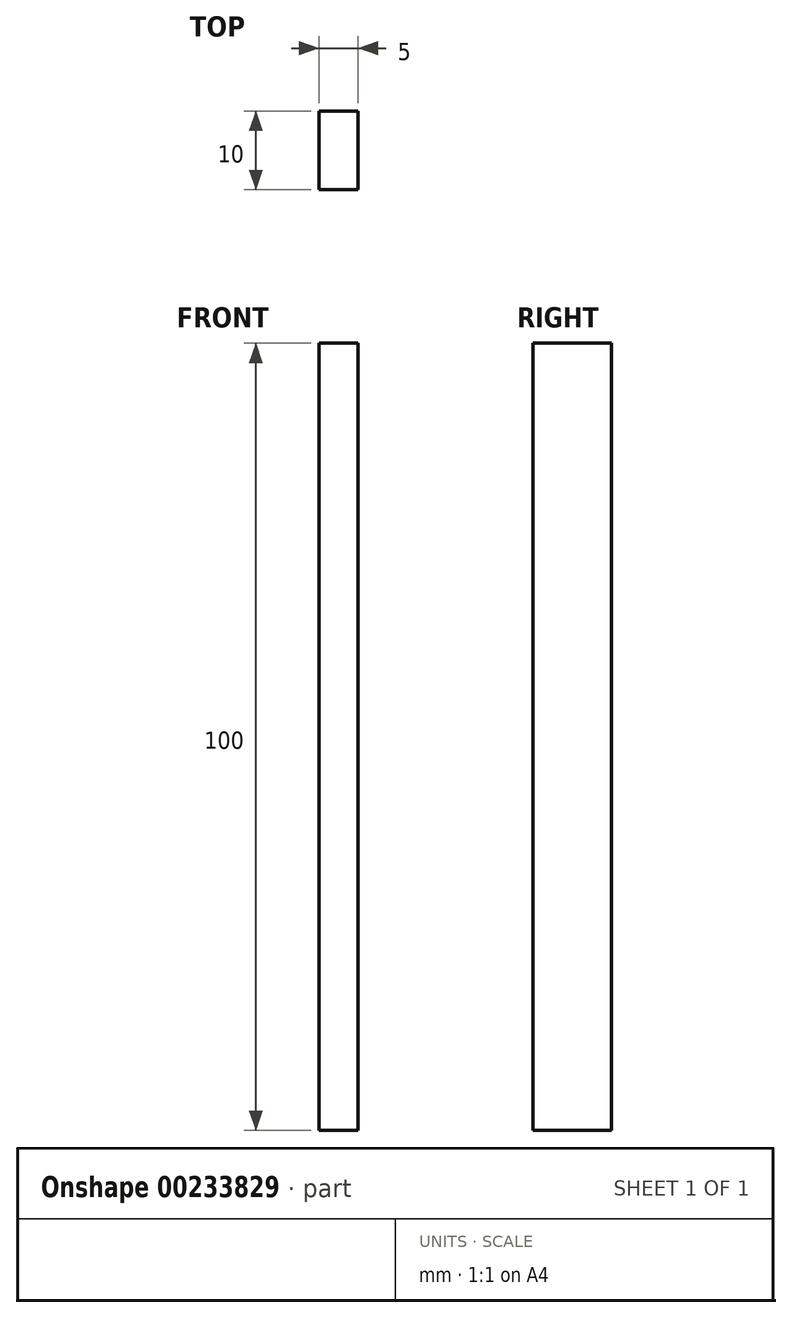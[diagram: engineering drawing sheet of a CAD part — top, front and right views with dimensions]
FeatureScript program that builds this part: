
annotation { "Feature Type Name" : "Feature", "Feature Type Description" : "" }
export const myFeature = defineFeature(function(context is Context, id is Id, definition is map)
    precondition{}
    {
        {
            var Q0;
            Q0=qCreatedBy(makeId("Front.planeOp"),FACE);
            var sketch = newSketch(context, id + "F0", { "sketchPlane" : qUnion([Q0])});
            skLineSegment(sketch, "E0.bottom", {"start": v(-5, 100) * mm, "end": v(0, 100) * mm});
            skLineSegment(sketch, "E0.top", {"start": v(-5, 0) * mm, "end": v(0, 0) * mm});
            skLineSegment(sketch, "E0.left", {"start": v(-5, 100) * mm, "end": v(-5, 0) * mm});
            skLineSegment(sketch, "E0.right", {"start": v(0, 100) * mm, "end": v(0, 0) * mm});
            skSolve(sketch);
        }
        {
            var Q0;
            Q0=makeQuery(id+"F0.imprint","IMPRINT",FACE,{"disambiguationData":[TD([[makeQuery(id+"F0.imprint","IMPRINT",EDGE,{"derivedFrom":sQuery(id+"F0.wireOp",EDGE,"E0.bottom")}),-1.0]])]});
            extrude(context, id + "F1", {"entities" : qUnion([Q0]), "depth" : 10 * mm});
        }
    });
